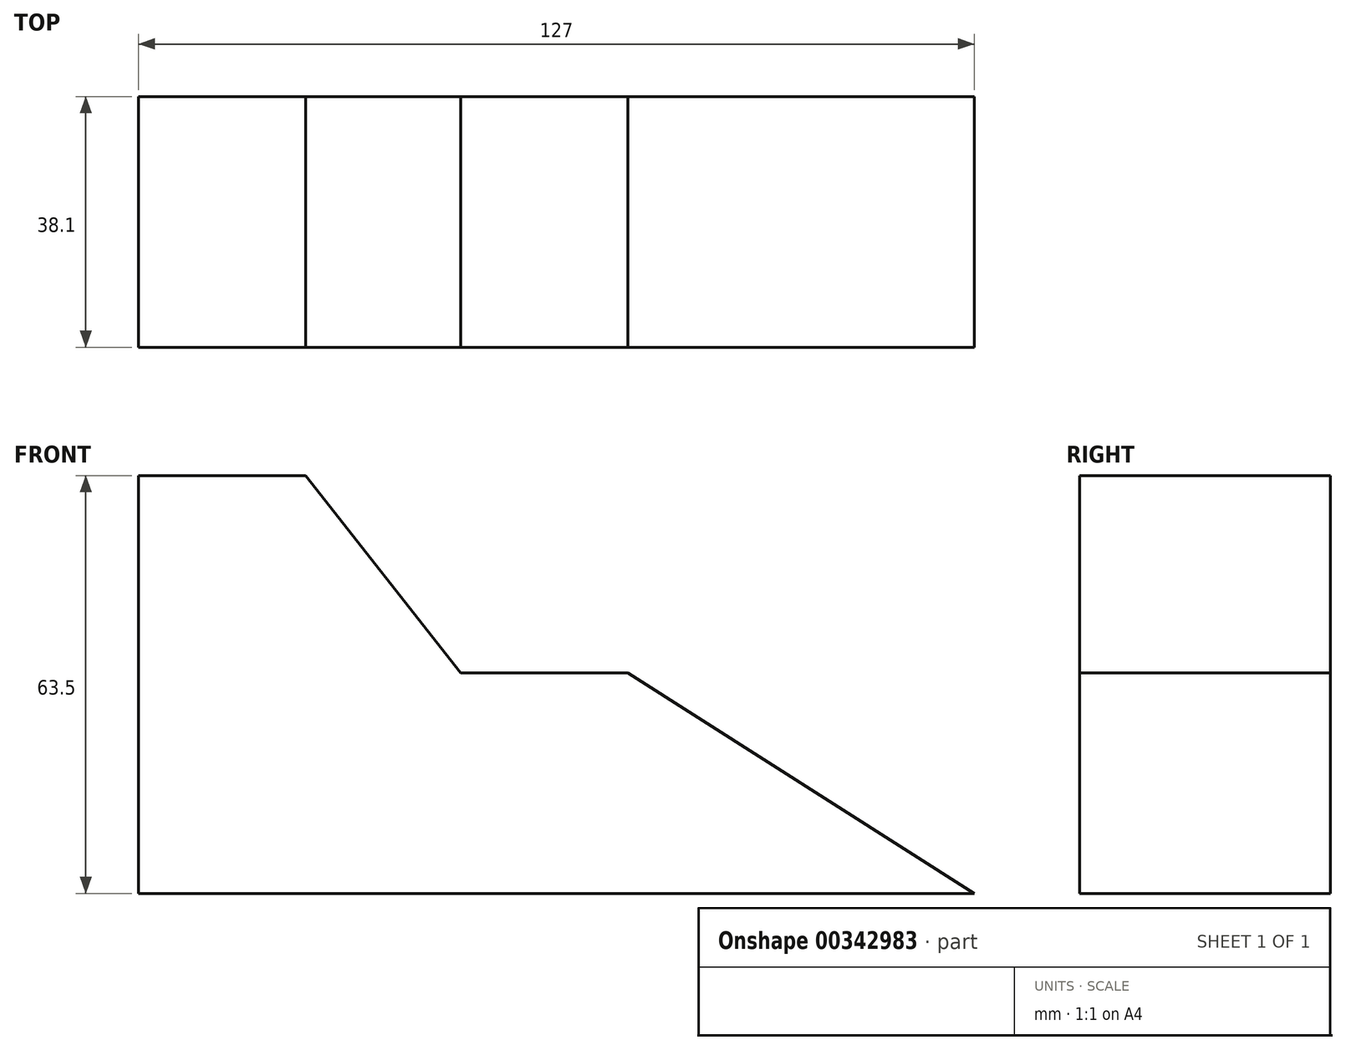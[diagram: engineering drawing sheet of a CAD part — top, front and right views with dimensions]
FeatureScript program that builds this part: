
annotation { "Feature Type Name" : "Feature", "Feature Type Description" : "" }
export const myFeature = defineFeature(function(context is Context, id is Id, definition is map)
    precondition{}
    {
        {
            var Q0;
            Q0=qCreatedBy(makeId("Front.planeOp"),FACE);
            var sketch = newSketch(context, id + "F0", { "sketchPlane" : qUnion([Q0])});
            skLineSegment(sketch, "E0", {"start": v(-66.7, -27.73) * mm, "end": v(60.3, -27.73) * mm});
            skLineSegment(sketch, "E1", {"start": v(-66.7, -27.73) * mm, "end": v(-66.7, 35.77) * mm});
            skLineSegment(sketch, "E2", {"start": v(-66.7, 35.77) * mm, "end": v(-41.3, 35.77) * mm});
            skLineSegment(sketch, "E3", {"start": v(-41.3, 35.77) * mm, "end": v(-17.76, 5.8) * mm});
            skLineSegment(sketch, "E4", {"start": v(-17.76, 5.8) * mm, "end": v(7.64, 5.8) * mm});
            skLineSegment(sketch, "E5", {"start": v(7.64, 5.8) * mm, "end": v(60.3, -27.73) * mm});
            skSolve(sketch);
        }
        {
            var Q0;
            Q0=makeQuery(id+"F0.imprint","IMPRINT",FACE,{"disambiguationData":[TD([[makeQuery(id+"F0.imprint","IMPRINT",EDGE,{"derivedFrom":sQuery(id+"F0.wireOp",EDGE,"E0")}),1.0]])]});
            extrude(context, id + "F1", {"entities" : qUnion([Q0]), "depth" : 38.1 * mm});
        }
    });
